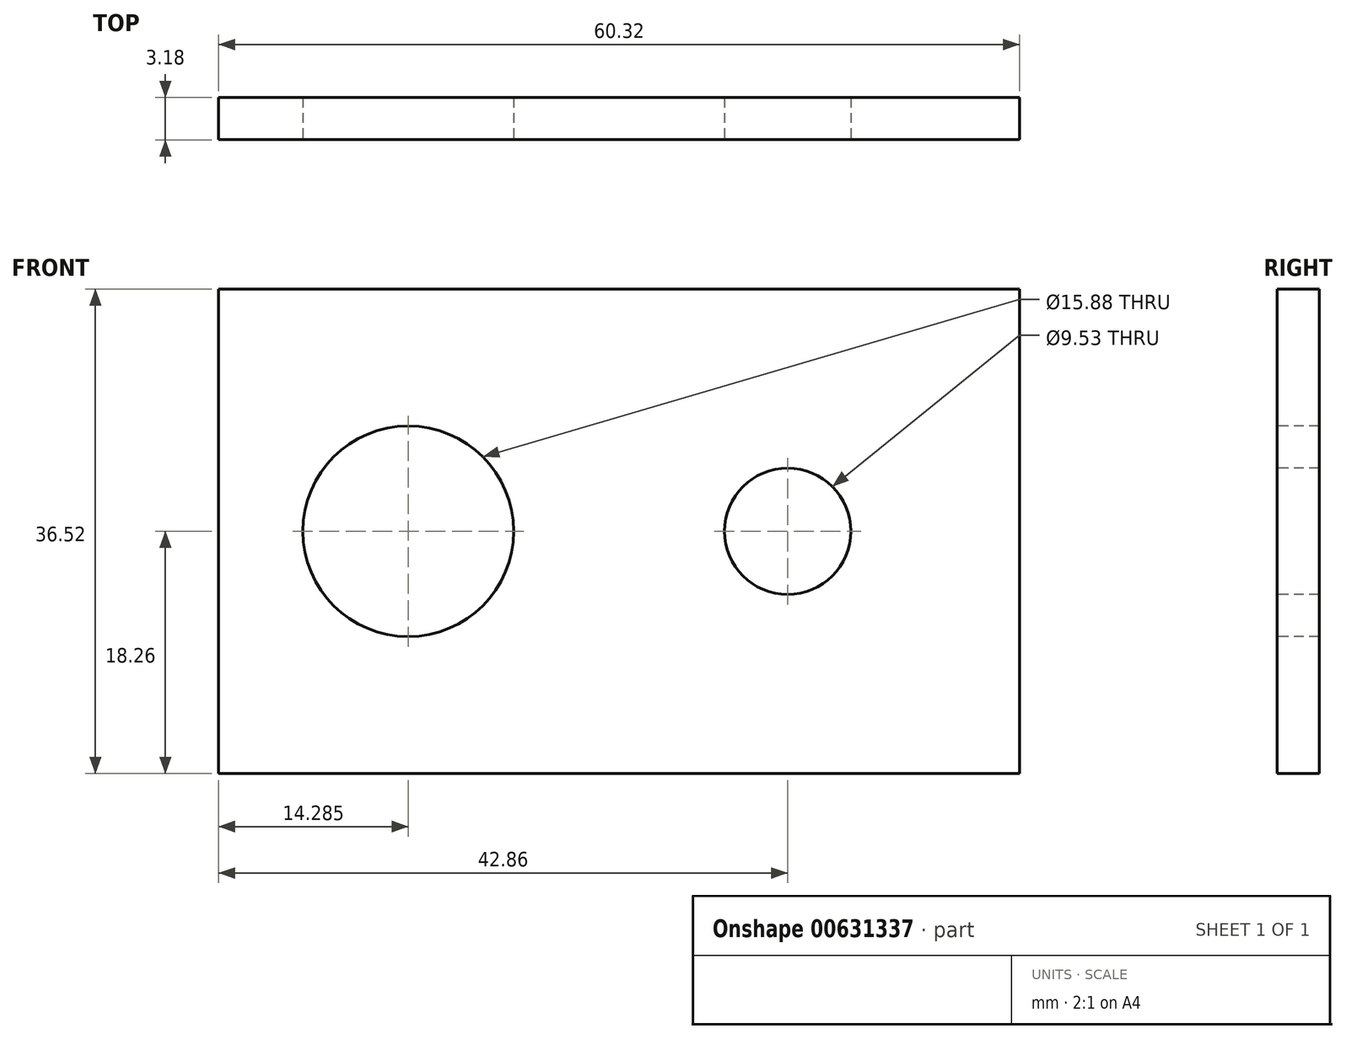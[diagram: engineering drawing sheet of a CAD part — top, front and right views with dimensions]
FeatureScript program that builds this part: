
annotation { "Feature Type Name" : "Feature", "Feature Type Description" : "" }
export const myFeature = defineFeature(function(context is Context, id is Id, definition is map)
    precondition{}
    {
        {
            var Q0;
            Q0=qCreatedBy(makeId("Front.planeOp"),FACE);
            var sketch = newSketch(context, id + "F0", { "sketchPlane" : qUnion([Q0])});
            skLineSegment(sketch, "E0.bottom", {"start": v(30.16, 18.26) * mm, "end": v(-30.16, 18.26) * mm});
            skLineSegment(sketch, "E0.top", {"start": v(30.16, -18.26) * mm, "end": v(-30.16, -18.26) * mm});
            skLineSegment(sketch, "E0.left", {"start": v(30.16, 18.26) * mm, "end": v(30.16, -18.26) * mm});
            skLineSegment(sketch, "E0.right", {"start": v(-30.16, 18.26) * mm, "end": v(-30.16, -18.26) * mm});
            skPoint(sketch, "E0.middle", {"position": v(0, 0) * mm});
            skSolve(sketch);
        }
        {
            var Q0;
            Q0 = qSketchRegion(id + "F0", true);
            extrude(context, id + "F1", {"entities" : qUnion([Q0]), "depth" : 3.17 * mm, "offsetDistance" : 25.4 * mm});
        }
        {
            var Q0;
            Q0=makeQuery(id+"F1.opExtrude","CAP_FACE",FACE,{"disambiguationData":[OSD([sQuery(id+"F0.wireOp",EDGE,"E0.bottom"),sQuery(id+"F0.wireOp",EDGE,"E0.top"),sQuery(id+"F0.wireOp",EDGE,"E0.left"),sQuery(id+"F0.wireOp",EDGE,"E0.right")])],"isStart":false});
            var sketch = newSketch(context, id + "F2", { "sketchPlane" : qUnion([Q0])});
            skPoint(sketch, "E1", {"position": v(-15.88, 0) * mm});
            skSolve(sketch);
        }
        {
            var Q0;
            Q0=sQuery(id+"F2.wireOp",VERTEX,"E1");
            var Q1;
            Q1=makeQuery(id+"F1.opExtrude","SWEPT_BODY",BODY,{"disambiguationData":[OSD([sQuery(id+"F0.wireOp",EDGE,"E0.bottom"),sQuery(id+"F0.wireOp",EDGE,"E0.top"),sQuery(id+"F0.wireOp",EDGE,"E0.left"),sQuery(id+"F0.wireOp",EDGE,"E0.right")])]});
            hole(context, id + "F3", {"style" : HoleStyle.SIMPLE, "endStyle" : HoleEndStyle.THROUGH, "holeDiameter" : 15.88 * mm, "majorDiameter" : 6.35 * mm, "isTappedThrough" : true, "tappedDepth" : 12.7 * mm, "tapClearance" : 3, "locations" : qUnion([Q0]), "scope" : qUnion([Q1])});
        }
        {
            var Q0;
            Q0=makeQuery(id+"F1.opExtrude","CAP_FACE",FACE,{"disambiguationData":[OSD([sQuery(id+"F0.wireOp",EDGE,"E0.bottom"),sQuery(id+"F0.wireOp",EDGE,"E0.top"),sQuery(id+"F0.wireOp",EDGE,"E0.left"),sQuery(id+"F0.wireOp",EDGE,"E0.right")])],"isStart":false});
            var sketch = newSketch(context, id + "F4", { "sketchPlane" : qUnion([Q0])});
            skPoint(sketch, "E2", {"position": v(12.7, 0) * mm});
            skSolve(sketch);
        }
        {
            var Q0;
            Q0=sQuery(id+"F4.wireOp",VERTEX,"E2");
            var Q1;
            Q1=makeQuery(id+"F1.opExtrude","SWEPT_BODY",BODY,{"disambiguationData":[OSD([sQuery(id+"F0.wireOp",EDGE,"E0.bottom"),sQuery(id+"F0.wireOp",EDGE,"E0.top"),sQuery(id+"F0.wireOp",EDGE,"E0.left"),sQuery(id+"F0.wireOp",EDGE,"E0.right")])]});
            hole(context, id + "F5", {"style" : HoleStyle.SIMPLE, "endStyle" : HoleEndStyle.THROUGH, "holeDiameter" : 9.52 * mm, "majorDiameter" : 6.35 * mm, "isTappedThrough" : true, "tappedDepth" : 12.7 * mm, "tapClearance" : 3, "locations" : qUnion([Q0]), "scope" : qUnion([Q1])});
        }
    });
